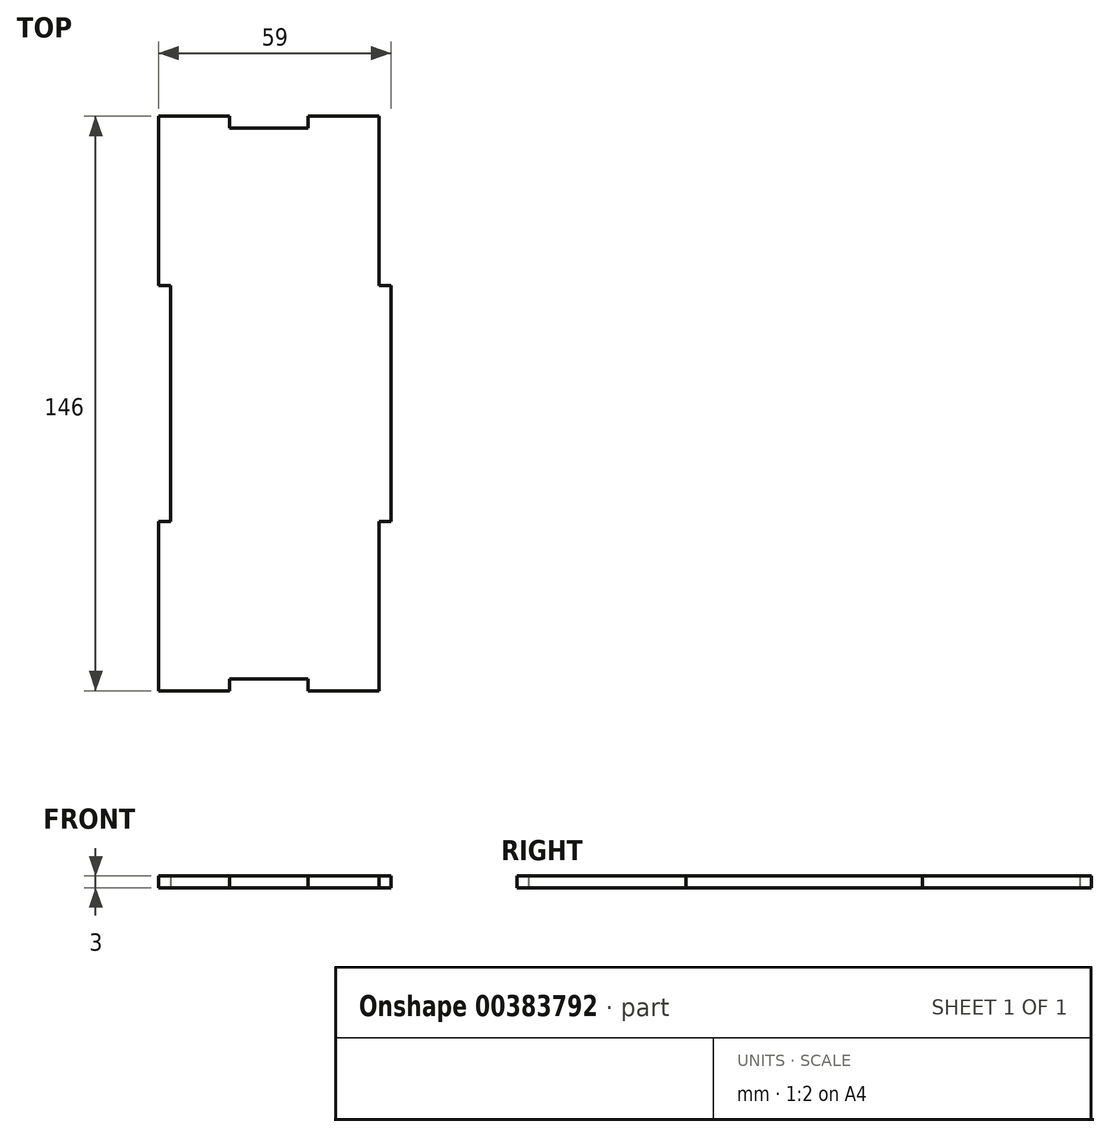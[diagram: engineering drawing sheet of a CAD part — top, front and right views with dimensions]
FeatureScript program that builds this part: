
annotation { "Feature Type Name" : "Feature", "Feature Type Description" : "" }
export const myFeature = defineFeature(function(context is Context, id is Id, definition is map)
    precondition{}
    {
        {
            var Q0;
            Q0=qCreatedBy(makeId("Top.planeOp"),FACE);
            var sketch = newSketch(context, id + "F0", { "sketchPlane" : qUnion([Q0])});
            skLineSegment(sketch, "E0.bottom", {"start": v(28, -73) * mm, "end": v(10, -73) * mm});
            skLineSegment(sketch, "E0.top", {"start": v(28, 73) * mm, "end": v(10, 73) * mm});
            skLineSegment(sketch, "E0.left", {"start": v(28, -73) * mm, "end": v(28, -30) * mm});
            skLineSegment(sketch, "E0.right", {"start": v(-28, -73) * mm, "end": v(-28, -30) * mm});
            skPoint(sketch, "E0.middle", {"position": v(0, 0) * mm});
            skLineSegment(sketch, "E1.bottom", {"start": v(-25, -30) * mm, "end": v(-28, -30) * mm});
            skLineSegment(sketch, "E1.top", {"start": v(-25, 30) * mm, "end": v(-31, 30) * mm});
            skLineSegment(sketch, "E1.left", {"start": v(-25, -30) * mm, "end": v(-25, 30) * mm});
            skPoint(sketch, "E1.middle", {"position": v(-28, 0) * mm});
            skLineSegment(sketch, "E2.trimOffspring", {"start": v(-28, 30) * mm, "end": v(-28, 73) * mm});
            skPoint(sketch, "E1.right.start.orphan", {"position": v(-31, -30) * mm});
            skLineSegment(sketch, "E3.bottom", {"start": v(31, -30) * mm, "end": v(28, -30) * mm});
            skLineSegment(sketch, "E3.top", {"start": v(31, 30) * mm, "end": v(28, 30) * mm});
            skLineSegment(sketch, "E3.left", {"start": v(31, -30) * mm, "end": v(31, 30) * mm});
            skPoint(sketch, "E3.middle", {"position": v(28, 0) * mm});
            skPoint(sketch, "E4.orphan", {"position": v(25, -30) * mm});
            skLineSegment(sketch, "E5.trimOffspring", {"start": v(28, 30) * mm, "end": v(28, 73) * mm});
            skPoint(sketch, "E6.orphan", {"position": v(25, 30) * mm});
            skPoint(sketch, "E7.middle", {"position": v(0, 73) * mm});
            skLineSegment(sketch, "E8.trimOffspring", {"start": v(-10, 73) * mm, "end": v(-28, 73) * mm});
            skPoint(sketch, "E7.top.end.orphan", {"position": v(-10, 70) * mm});
            skPoint(sketch, "E7.top.start.orphan", {"position": v(10, 70) * mm});
            skPoint(sketch, "E9.middle", {"position": v(0, -73) * mm});
            skLineSegment(sketch, "E10.trimOffspring", {"start": v(-10, -73) * mm, "end": v(-28, -73) * mm});
            skLineSegment(sketch, "E11", {"start": v(-10, 73) * mm, "end": v(-10, 70) * mm});
            skLineSegment(sketch, "E12", {"start": v(-10, 70) * mm, "end": v(10, 70) * mm});
            skLineSegment(sketch, "E13", {"start": v(10, 70) * mm, "end": v(10, 73) * mm});
            skPoint(sketch, "E7.right.start.orphan", {"position": v(-10, 76) * mm});
            skPoint(sketch, "E7.left.start.orphan", {"position": v(10, 76) * mm});
            skPoint(sketch, "E9.right.end.orphan", {"position": v(-7, -76) * mm});
            skPoint(sketch, "E9.left.end.orphan", {"position": v(13, -76) * mm});
            skLineSegment(sketch, "E14", {"start": v(-10, -73) * mm, "end": v(-10, -70) * mm});
            skLineSegment(sketch, "E15", {"start": v(-10, -70) * mm, "end": v(10, -70) * mm});
            skLineSegment(sketch, "E16", {"start": v(10, -70) * mm, "end": v(10, -73) * mm});
            skSolve(sketch);
        }
        {
            var Q0;
            Q0=qSketchRegion(id+"F0",true);
            extrude(context, id + "F1", {"entities" : qUnion([Q0]), "depth" : 3 * mm});
        }
    });
